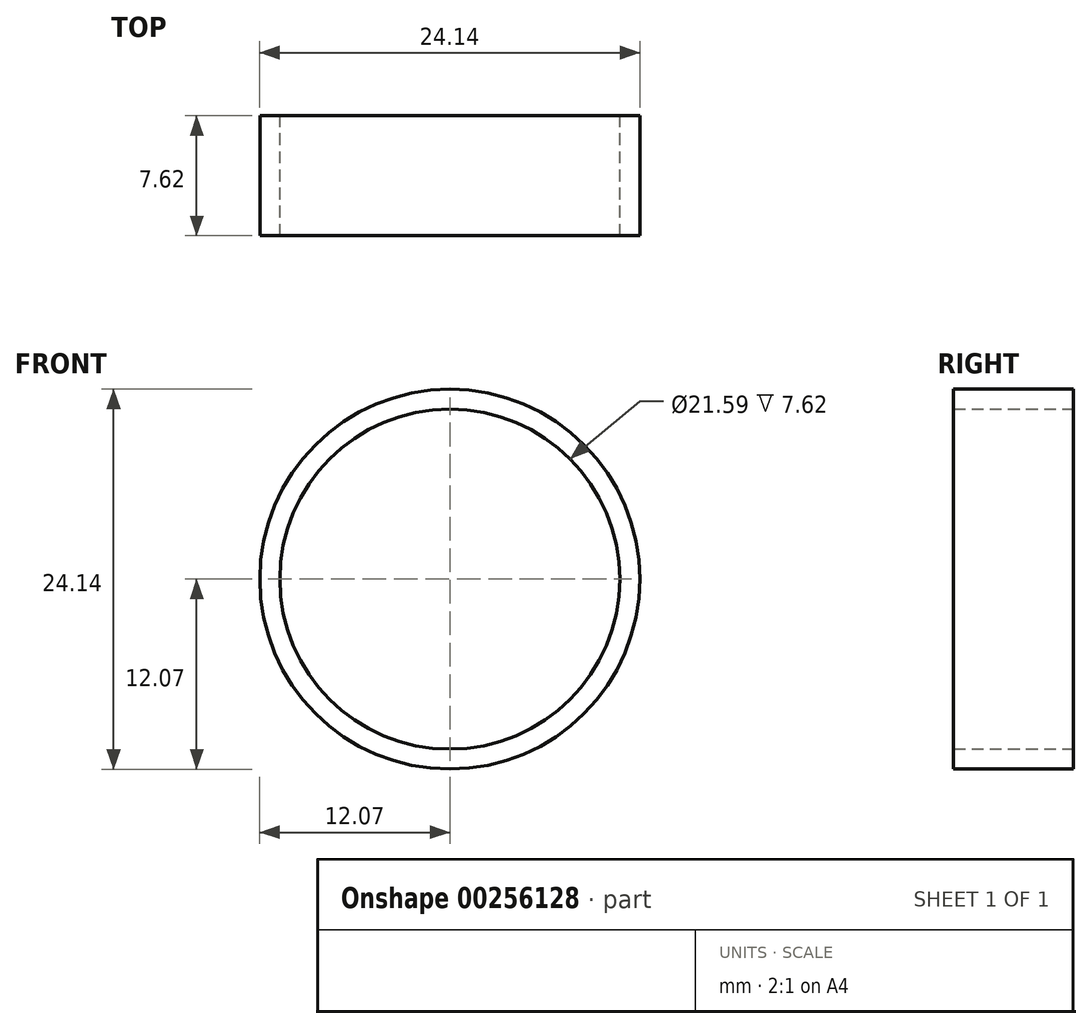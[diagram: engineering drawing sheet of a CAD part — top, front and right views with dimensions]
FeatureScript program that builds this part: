
annotation { "Feature Type Name" : "Feature", "Feature Type Description" : "" }
export const myFeature = defineFeature(function(context is Context, id is Id, definition is map)
    precondition{}
    {
        {
            var Q0;
            Q0=qCreatedBy(makeId("Front.planeOp"),FACE);
            var sketch = newSketch(context, id + "F0", { "sketchPlane" : qUnion([Q0])});
            skCircle(sketch, "E0", {"center": v(0, 0) * mm, "radius": 10.8 * mm});
            skCircle(sketch, "E1.0", {"center": v(0, 0) * mm, "radius": 12.07 * mm});
            skSolve(sketch);
        }
        {
            var Q0;
            Q0=makeQuery(id+"F0.imprint","IMPRINT",FACE,{"disambiguationData":[TD([[makeQuery(id+"F0.imprint","IMPRINT",EDGE,{"derivedFrom":sQuery(id+"F0.wireOp",EDGE,"E0")}),-1.0]])]});
            extrude(context, id + "F1", {"entities" : qUnion([Q0]), "depth" : 7.62 * mm});
        }
    });
